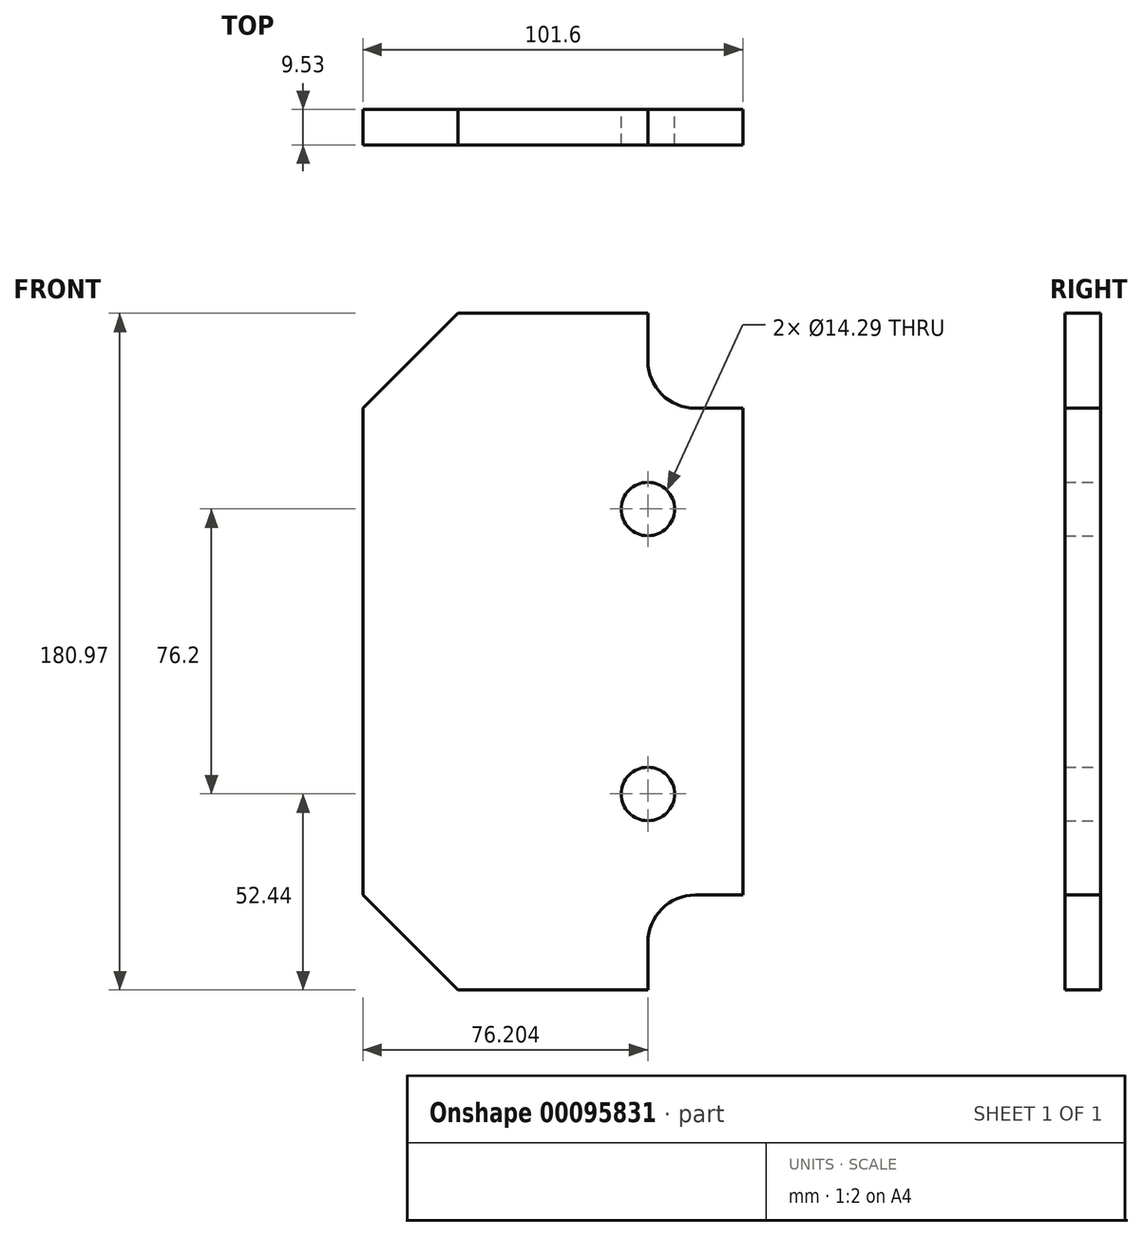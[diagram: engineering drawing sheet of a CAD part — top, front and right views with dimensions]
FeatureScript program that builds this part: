
annotation { "Feature Type Name" : "Feature", "Feature Type Description" : "" }
export const myFeature = defineFeature(function(context is Context, id is Id, definition is map)
    precondition{}
    {
        {
            var Q0;
            Q0=qCreatedBy(makeId("Front.planeOp"),FACE);
            var sketch = newSketch(context, id + "F1", { "sketchPlane" : qUnion([Q0]), "disableImprinting" : false});
            skLineSegment(sketch, "E0", {"start": v(5.03, 65.03) * mm, "end": v(5.03, -65.14) * mm});
            skLineSegment(sketch, "E1", {"start": v(5.03, -65.14) * mm, "end": v(30.43, -90.54) * mm});
            skLineSegment(sketch, "E2", {"start": v(30.43, -90.54) * mm, "end": v(81.23, -90.54) * mm});
            skLineSegment(sketch, "E3", {"start": v(81.23, 90.43) * mm, "end": v(30.43, 90.43) * mm});
            skLineSegment(sketch, "E4", {"start": v(30.43, 90.43) * mm, "end": v(5.03, 65.03) * mm});
            skLineSegment(sketch, "E5", {"start": v(81.23, 90.43) * mm, "end": v(81.23, 90.43) * mm});
            skLineSegment(sketch, "E6", {"start": v(81.23, 77.73) * mm, "end": v(81.23, 90.43) * mm});
            skLineSegment(sketch, "E7", {"start": v(106.63, 65.03) * mm, "end": v(93.93, 65.03) * mm});
            skLineSegment(sketch, "E8", {"start": v(106.63, -65.14) * mm, "end": v(106.63, 65.03) * mm});
            skLineSegment(sketch, "E9", {"start": v(106.63, -65.14) * mm, "end": v(93.93, -65.14) * mm});
            skLineSegment(sketch, "E10", {"start": v(81.23, -77.84) * mm, "end": v(81.23, -90.54) * mm});
            skPoint(sketch, "E11.visualSharp", {"position": v(81.23, 65.03) * mm});
            skArc(sketch, "E11.filletArc", {"start": v(81.23, 77.73) * mm, "mid": v(84.95, 68.75) * mm, "end": v(93.93, 65.03) * mm});
            skPoint(sketch, "E12.visualSharp", {"position": v(81.23, -65.14) * mm});
            skArc(sketch, "E12.filletArc", {"start": v(93.93, -65.14) * mm, "mid": v(84.95, -68.86) * mm, "end": v(81.23, -77.84) * mm});
            skCircle(sketch, "E13", {"center": v(81.23, 38.1) * mm, "radius": 7.14 * mm});
            skPoint(sketch, "E14.orphan", {"position": v(5.03, 0) * mm});
            skLineSegment(sketch, "E15", {"start": v(0, 0) * mm, "end": v(84.96, 0) * mm});
            skCircle(sketch, "E16.MirrorC", {"center": v(81.23, -38.1) * mm, "radius": 7.14 * mm});
            skSolve(sketch);
        }
        {
            var Q0;
            Q0=makeQuery(id+"F1.imprint","IMPRINT",FACE,{"disambiguationData":[TD([[makeQuery(id+"F1.imprint","IMPRINT",EDGE,{"derivedFrom":sQuery(id+"F1.wireOp",EDGE,"E0")}),1.0]])]});
            extrude(context, id + "F0", {"entities" : qUnion([Q0]), "depth" : 9.52 * mm});
        }
    });
